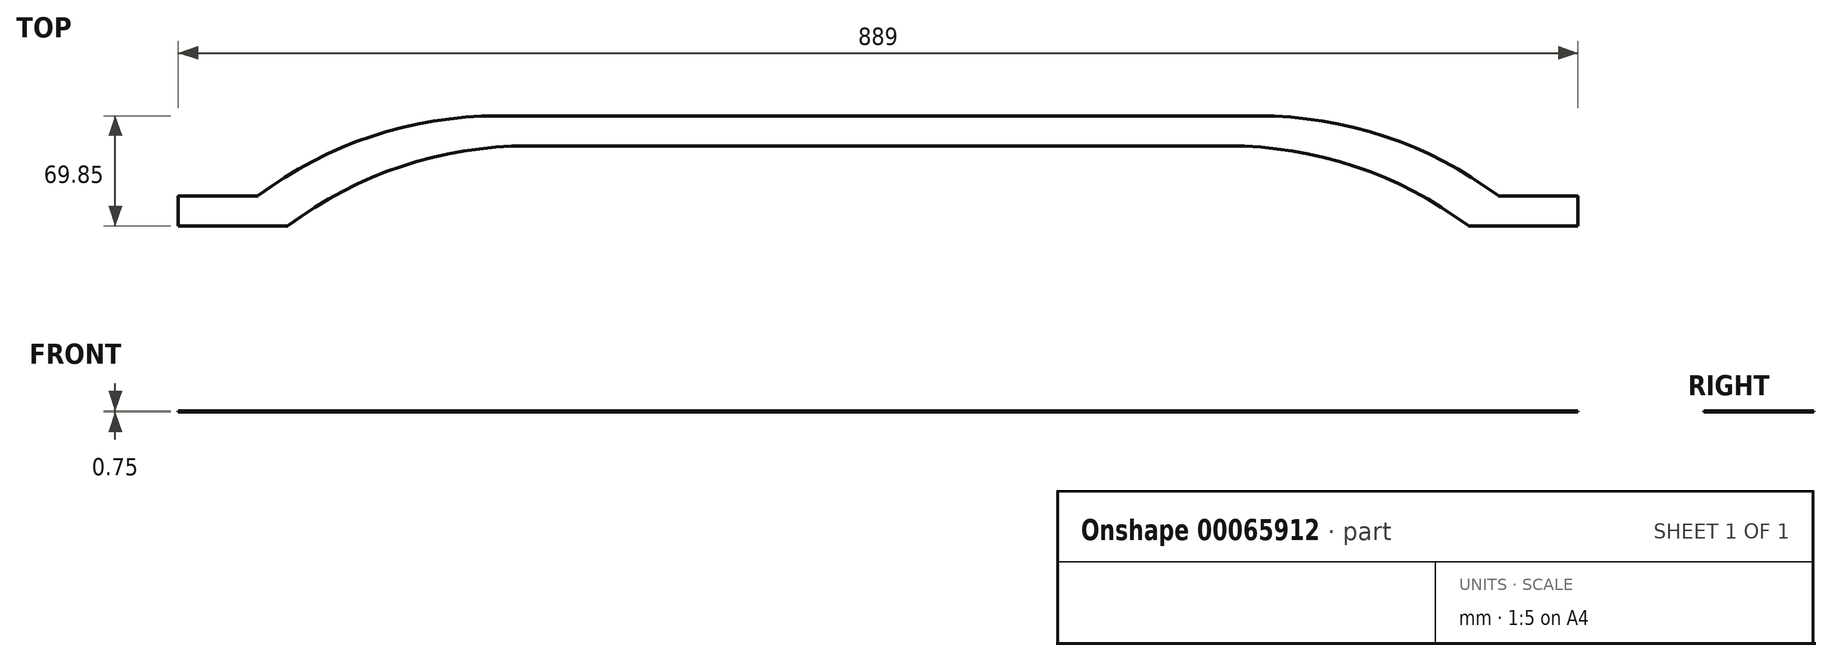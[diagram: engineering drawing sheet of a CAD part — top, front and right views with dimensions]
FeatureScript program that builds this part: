
annotation { "Feature Type Name" : "Feature", "Feature Type Description" : "" }
export const myFeature = defineFeature(function(context is Context, id is Id, definition is map)
    precondition{}
    {
        {
            assignVariable(context, id + "F0", {"name" : "MaterialThickness", "anyValue" : .75});
        }
        {
            assignVariable(context, id + "F1", {"name" : "Thickness", "anyValue" : .75});
        }
        {
            var Q0;
            Q0=qCreatedBy(makeId("Top.planeOp"),FACE);
            var sketch = newSketch(context, id + "F2", { "sketchPlane" : qUnion([Q0])});
            skLineSegment(sketch, "E0", {"start": v(0, 0) * mm, "end": v(69.85, 0) * mm});
            skLineSegment(sketch, "E1", {"start": v(69.85, 0) * mm, "end": v(69.85, 50.8) * mm});
            skLineSegment(sketch, "E2", {"start": v(69.85, 50.8) * mm, "end": v(444.5, 50.8) * mm});
            skLineSegment(sketch, "E3", {"start": v(0, 0) * mm, "end": v(0, 19.05) * mm});
            skLineSegment(sketch, "E4", {"start": v(0, 19.05) * mm, "end": v(50.8, 19.05) * mm});
            skLineSegment(sketch, "E5", {"start": v(50.8, 19.05) * mm, "end": v(50.8, 69.85) * mm});
            skLineSegment(sketch, "E6", {"start": v(50.8, 69.85) * mm, "end": v(444.5, 69.85) * mm});
            skLineSegment(sketch, "E7", {"start": v(444.5, 94.65) * mm, "end": v(444.5, 0) * mm, "construction": true});
            skLineSegment(sketch, "E8.MirrorCS", {"start": v(889, 0) * mm, "end": v(889, 19.05) * mm});
            skLineSegment(sketch, "E9.MirrorCS", {"start": v(838.2, 19.05) * mm, "end": v(838.2, 69.85) * mm});
            skLineSegment(sketch, "E10.MirrorCS", {"start": v(838.2, 69.85) * mm, "end": v(444.5, 69.85) * mm});
            skLineSegment(sketch, "E11.MirrorCS", {"start": v(819.15, 50.8) * mm, "end": v(444.5, 50.8) * mm});
            skLineSegment(sketch, "E12.MirrorCS", {"start": v(819.15, 0) * mm, "end": v(819.15, 50.8) * mm});
            skLineSegment(sketch, "E13.MirrorCS", {"start": v(889, 0) * mm, "end": v(819.15, 0) * mm});
            skLineSegment(sketch, "E14.MirrorCS", {"start": v(889, 19.05) * mm, "end": v(838.2, 19.05) * mm});
            skSolve(sketch);
        }
        {
            var Q0;
            Q0=makeQuery(id+"F2.imprint","IMPRINT",FACE,{"disambiguationData":[TD([[makeQuery(id+"F2.imprint","IMPRINT",EDGE,{"derivedFrom":sQuery(id+"F2.wireOp",EDGE,"E0")}),1.0]])]});
            extrude(context, id + "F3", {"entities" : qUnion([Q0]), "depth" : (getVariable(context, 'MaterialThickness')) * mm});
        }
        {
            var Q0;
            Q0=makeQuery(id+"F3.opExtrude","SWEPT_EDGE",EDGE,{"disambiguationData":[OSD([sQuery(id+"F2.wireOp",EDGE,"E0"),sQuery(id+"F2.wireOp",EDGE,"E1")])]});
            var Q1;
            Q1=makeQuery(id+"F3.opExtrude","SWEPT_EDGE",EDGE,{"disambiguationData":[OSD([sQuery(id+"F2.wireOp",EDGE,"E4"),sQuery(id+"F2.wireOp",EDGE,"E5")])]});
            var Q2;
            Q2=makeQuery(id+"F3.opExtrude","SWEPT_EDGE",EDGE,{"disambiguationData":[OSD([sQuery(id+"F2.wireOp",EDGE,"E12.MirrorCS"),sQuery(id+"F2.wireOp",EDGE,"E13.MirrorCS")])]});
            var Q3;
            Q3=makeQuery(id+"F3.opExtrude","SWEPT_EDGE",EDGE,{"disambiguationData":[OSD([sQuery(id+"F2.wireOp",EDGE,"E9.MirrorCS"),sQuery(id+"F2.wireOp",EDGE,"E14.MirrorCS")])]});
            var Q4;
            Q4=makeQuery(id+"F3.opExtrude","SWEPT_EDGE",EDGE,{"disambiguationData":[OSD([sQuery(id+"F2.wireOp",EDGE,"E3"),sQuery(id+"F2.wireOp",EDGE,"E4")])]});
            var Q5;
            Q5=makeQuery(id+"F3.opExtrude","SWEPT_EDGE",EDGE,{"disambiguationData":[OSD([sQuery(id+"F2.wireOp",EDGE,"E8.MirrorCS"),sQuery(id+"F2.wireOp",EDGE,"E14.MirrorCS")])]});
            fillet(context, id + "F4", {"entities" : qUnion([Q0, Q1, Q2, Q3, Q4, Q5]), "radius" : (getVariable(context, 'Thickness') / 2) * mm, "tangentPropagation" : true, "allowEdgeOverflow" : false});
        }
        {
            var Q0;
            Q0=makeQuery(id+"F3.opExtrude","SWEPT_EDGE",EDGE,{"disambiguationData":[OSD([sQuery(id+"F2.wireOp",EDGE,"E1"),sQuery(id+"F2.wireOp",EDGE,"E2")])]});
            var Q1;
            Q1=makeQuery(id+"F3.opExtrude","SWEPT_EDGE",EDGE,{"disambiguationData":[OSD([sQuery(id+"F2.wireOp",EDGE,"E5"),sQuery(id+"F2.wireOp",EDGE,"E6")])]});
            var Q2;
            Q2=makeQuery(id+"F3.opExtrude","SWEPT_EDGE",EDGE,{"disambiguationData":[OSD([sQuery(id+"F2.wireOp",EDGE,"E11.MirrorCS"),sQuery(id+"F2.wireOp",EDGE,"E12.MirrorCS")])]});
            var Q3;
            Q3=makeQuery(id+"F3.opExtrude","SWEPT_EDGE",EDGE,{"disambiguationData":[OSD([sQuery(id+"F2.wireOp",EDGE,"E9.MirrorCS"),sQuery(id+"F2.wireOp",EDGE,"E10.MirrorCS")])]});
            fillet(context, id + "F5", {"entities" : qUnion([Q0, Q1, Q2, Q3]), "radius" : 254 * mm, "tangentPropagation" : true, "allowEdgeOverflow" : false});
        }
    });
